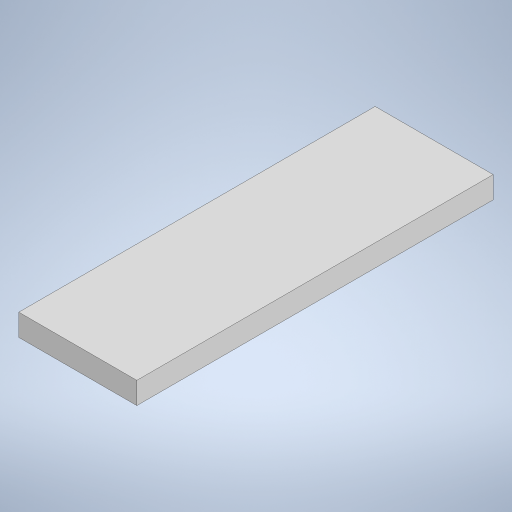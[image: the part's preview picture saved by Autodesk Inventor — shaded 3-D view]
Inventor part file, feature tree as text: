
AUTODESK INVENTOR PART (.ipt)
format: ipt  version: 2023 (Build 270158000, 158)  size: 204,288 bytes
history: native  units: mm
features: other x1, extrude x1, sketch x1
ambient origin geometry x8: Origin, YZ Plane, XZ Plane, XY Plane, X Axis, Y Axis, Z Axis, Center Point
bodies: Body1 (feature_tree)
feature tree (3):
  other  "Sólido1"
  extrude  "Extrusión1"  Depth=163.0mm
  sketch  "Boceto1"  dims[d0=54.0mm d1=163.0mm d2=10.0mm d3=0.0mm]
